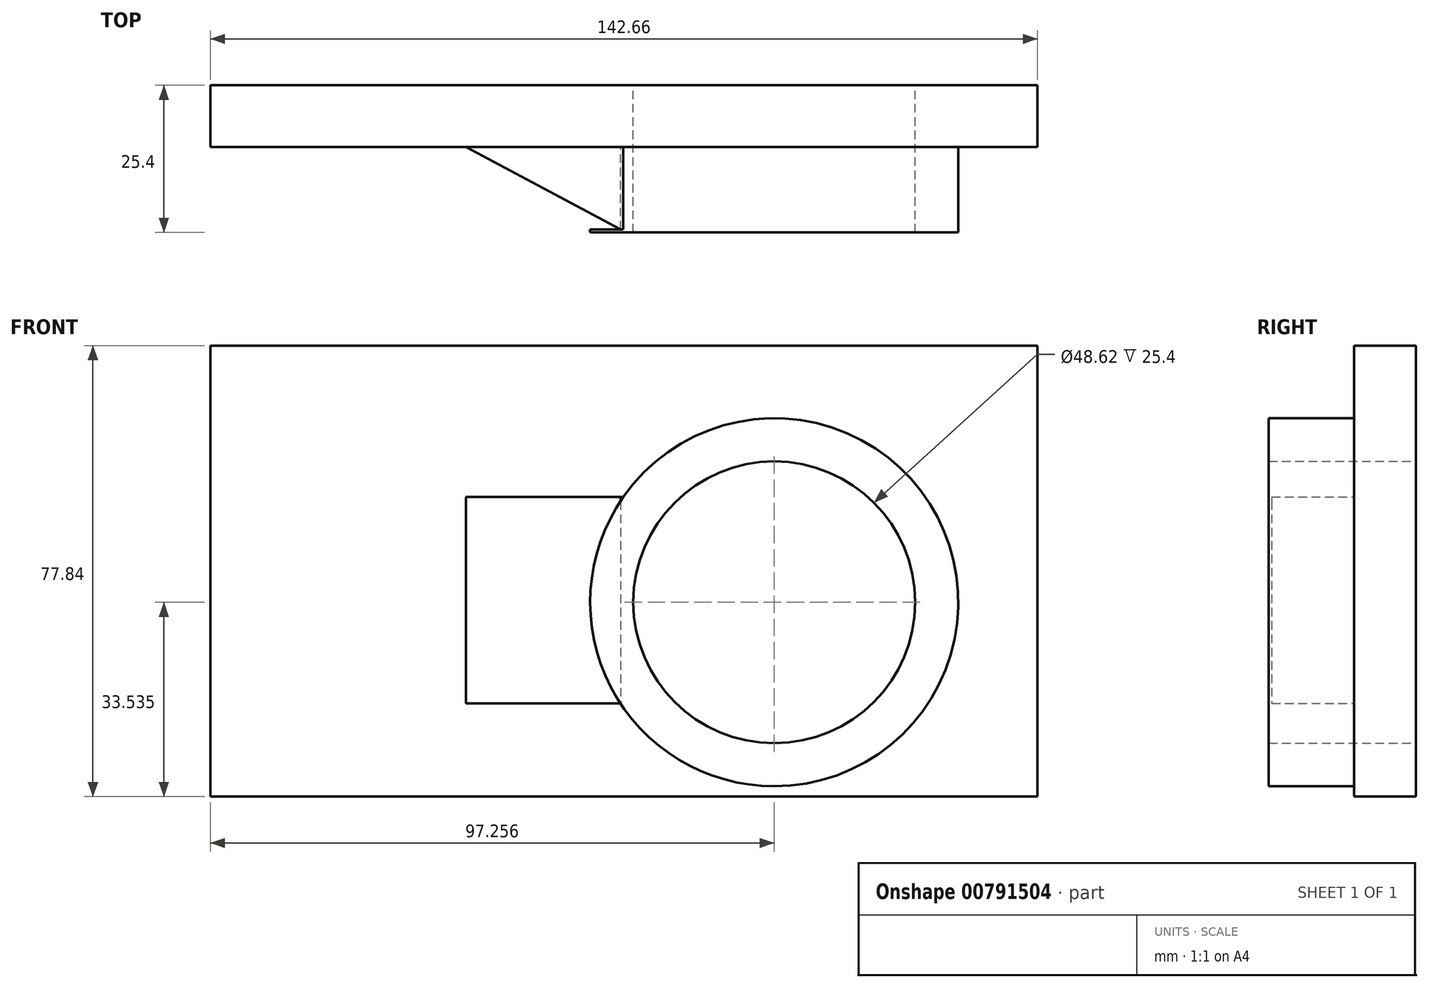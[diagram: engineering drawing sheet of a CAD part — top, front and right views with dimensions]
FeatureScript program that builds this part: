
annotation { "Feature Type Name" : "Feature", "Feature Type Description" : "" }
export const myFeature = defineFeature(function(context is Context, id is Id, definition is map)
    precondition{}
    {
        {
            var Q0;
            Q0=qCreatedBy(makeId("Front.planeOp"),FACE);
            var sketch = newSketch(context, id + "F0", { "sketchPlane" : qUnion([Q0])});
            skLineSegment(sketch, "E0.bottom", {"start": v(-71.21, -28.56) * mm, "end": v(71.45, -28.56) * mm});
            skLineSegment(sketch, "E0.top", {"start": v(-71.21, 49.28) * mm, "end": v(71.45, 49.28) * mm});
            skLineSegment(sketch, "E0.left", {"start": v(-71.21, -28.56) * mm, "end": v(-71.21, 49.28) * mm});
            skLineSegment(sketch, "E0.right", {"start": v(71.45, -28.56) * mm, "end": v(71.45, 49.28) * mm});
            skSolve(sketch);
        }
        {
            var Q0;
            Q0=qCreatedBy(makeId("Front.planeOp"),FACE);
            var sketch = newSketch(context, id + "F1", { "sketchPlane" : qUnion([Q0])});
            skCircle(sketch, "E1", {"center": v(26.05, 4.98) * mm, "radius": 31.75 * mm});
            skCircle(sketch, "E2", {"center": v(26.05, 4.98) * mm, "radius": 24.3 * mm});
            skSolve(sketch);
        }
        {
            var Q0;
            Q0 = qSketchRegion(id + "F1", true);
            extrude(context, id + "F2", {"entities" : qUnion([Q0]), "depth" : 25.4 * mm, "offsetDistance" : 25.4 * mm});
        }
        {
            var Q0;
            Q0=makeQuery(id+"F0.imprint","IMPRINT",FACE,{"disambiguationData":[TD([[makeQuery(id+"F0.imprint","IMPRINT",EDGE,{"derivedFrom":sQuery(id+"F0.wireOp",EDGE,"E0.bottom")}),1.0]])]});
            extrude(context, id + "F3", {"entities" : qUnion([Q0]), "operationType" : NewBodyOperationType.ADD, "depth" : 10.67 * mm, "offsetDistance" : 25.4 * mm});
        }
        {
            var Q0;
            {var subQ0=sQuery(id+"F0.wireOp",EDGE,"E0.top");var subQ1=sQuery(id+"F0.wireOp",EDGE,"E0.bottom");var subQ2=sQuery(id+"F0.wireOp",EDGE,"E0.left");var subQ3=sQuery(id+"F0.wireOp",EDGE,"E0.right");Q0=makeQuery(id+"F3.boolean.opBoolean","SPLIT",FACE,{"disambiguationData":[TD([makeQuery(id+"F2.opExtrude","SWEPT_FACE",FACE,{"disambiguationData":[OSD([sQuery(id+"F1.wireOp",EDGE,"E1")])]})])],"derivedFrom":makeQuery(id+"F3.opExtrude","CAP_FACE",FACE,{"disambiguationData":[OSD([subQ1,subQ0,subQ2,subQ3])],"isStart":false})});}
            var sketch = newSketch(context, id + "F4", { "sketchPlane" : qUnion([Q0])});
            skLineSegment(sketch, "E3", {"start": v(0, 23.13) * mm, "end": v(-27.1, 23.13) * mm});
            skLineSegment(sketch, "E4", {"start": v(-27.1, 23.13) * mm, "end": v(-27.1, -12.47) * mm});
            skLineSegment(sketch, "E5", {"start": v(-27.1, -12.47) * mm, "end": v(-0.48, -12.47) * mm});
            skSolve(sketch);
        }
        {
            var Q0;
            Q0 = qSketchRegion(id + "F4", true);
            var Q1;
            {var subQ0=sQuery(id+"F4.wireOp",EDGE,"E3");Q1=makeQuery(id+"F4.imprint","IMPRINT",FACE,{"disambiguationData":[TD([[makeQuery(id+"F4.imprint","IMPRINT",EDGE,{"derivedFrom":subQ0}),1.0]])]});}
            extrude(context, id + "F5", {"entities" : qUnion([Q0, Q1]), "operationType" : NewBodyOperationType.ADD, "depth" : 14.22 * mm, "offsetDistance" : 25.4 * mm});
        }
        {
            var Q0;
            Q0=makeQuery(id+"F5.opExtrude","SWEPT_FACE",FACE,{"disambiguationData":[OSD([sQuery(id+"F4.wireOp",EDGE,"E5")])]});
            var sketch = newSketch(context, id + "F6", { "sketchPlane" : qUnion([Q0])});
            skLineSegment(sketch, "E6", {"start": v(-0.48, 24.9) * mm, "end": v(-27.1, 10.67) * mm});
            skSolve(sketch);
        }
        {
            var Q0;
            Q0=makeQuery(id+"F6.imprint","IMPRINT",FACE,{"disambiguationData":[TD([[makeQuery(id+"F6.imprint","IMPRINT",EDGE,{"derivedFrom":sQuery(id+"F6.wireOp",EDGE,"E6")}),-1.0]])]});
            extrude(context, id + "F7", {"entities" : qUnion([Q0]), "operationType" : NewBodyOperationType.REMOVE, "oppositeDirection" : true, "depth" : 37.85 * mm, "offsetDistance" : 25.4 * mm});
        }
        {
            var Q0;
            Q0=makeQuery(id+"F3.boolean.opBoolean","SPLIT",FACE,{"disambiguationData":[TD([makeQuery(id+"F2.opExtrude","SWEPT_FACE",FACE,{"disambiguationData":[OSD([sQuery(id+"F1.wireOp",EDGE,"E2")])]})])],"derivedFrom":makeQuery(id+"F3.opExtrude","CAP_FACE",FACE,{"disambiguationData":[OSD([sQuery(id+"F0.wireOp",EDGE,"E0.bottom"),sQuery(id+"F0.wireOp",EDGE,"E0.top"),sQuery(id+"F0.wireOp",EDGE,"E0.left"),sQuery(id+"F0.wireOp",EDGE,"E0.right")])],"isStart":false})});
            extrude(context, id + "F8", {"entities" : qUnion([Q0]), "operationType" : NewBodyOperationType.REMOVE, "oppositeDirection" : true, "depth" : 25.4 * mm, "offsetDistance" : 25.4 * mm});
        }
    });
